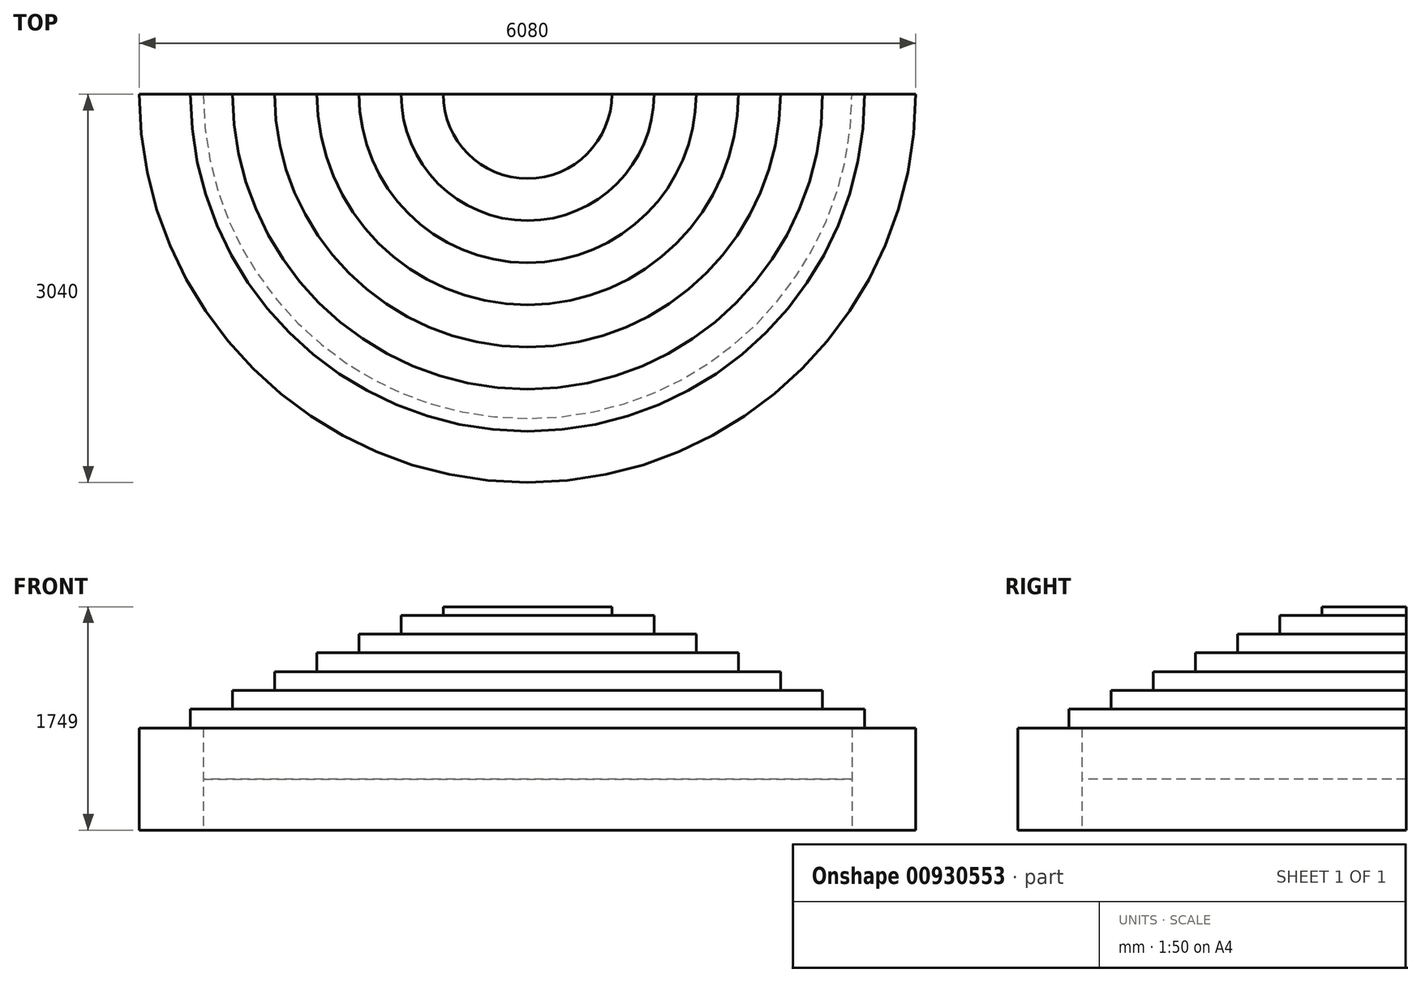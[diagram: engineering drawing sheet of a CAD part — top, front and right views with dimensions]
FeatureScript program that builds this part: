
annotation { "Feature Type Name" : "Feature", "Feature Type Description" : "" }
export const myFeature = defineFeature(function(context is Context, id is Id, definition is map)
    precondition{}
    {
        {
            var Q0;
            Q0=qCreatedBy(makeId("Front.planeOp"),FACE);
            var sketch = newSketch(context, id + "F0", { "sketchPlane" : qUnion([Q0])});
            skLineSegment(sketch, "E0", {"start": v(-660, 882) * mm, "end": v(-990, 882) * mm});
            skLineSegment(sketch, "E1", {"start": v(-990, 882) * mm, "end": v(-990, 735) * mm});
            skLineSegment(sketch, "E2", {"start": v(-990, 735) * mm, "end": v(-1320, 735) * mm});
            skLineSegment(sketch, "E3", {"start": v(-1320, 735) * mm, "end": v(-1320, 588) * mm});
            skLineSegment(sketch, "E4", {"start": v(-1320, 588) * mm, "end": v(-1650, 588) * mm});
            skLineSegment(sketch, "E5", {"start": v(-1650, 588) * mm, "end": v(-1650, 441) * mm});
            skLineSegment(sketch, "E6", {"start": v(-1650, 441) * mm, "end": v(-1980, 441) * mm});
            skLineSegment(sketch, "E7", {"start": v(-1980, 441) * mm, "end": v(-1980, 294) * mm});
            skLineSegment(sketch, "E8", {"start": v(-1980, 294) * mm, "end": v(-2310, 294) * mm});
            skLineSegment(sketch, "E9", {"start": v(-2310, 294) * mm, "end": v(-2310, 147) * mm});
            skLineSegment(sketch, "E10", {"start": v(-2310, 147) * mm, "end": v(-2640, 147) * mm});
            skLineSegment(sketch, "E11", {"start": v(-2640, 147) * mm, "end": v(-2640, 0) * mm});
            skLineSegment(sketch, "E12", {"start": v(-2640, 0) * mm, "end": v(0, 0) * mm});
            skLineSegment(sketch, "E13", {"start": v(0, 0) * mm, "end": v(0, 949) * mm});
            skLineSegment(sketch, "E14", {"start": v(-660, 882) * mm, "end": v(-660, 949) * mm});
            skLineSegment(sketch, "E15", {"start": v(-660, 949) * mm, "end": v(0, 949) * mm});
            skSolve(sketch);
        }
        {
            var Q0;
            Q0 = qSketchRegion(id + "F0", true);
            var Q1;
            Q1=sQuery(id+"F0.wireOp",EDGE,"E13");
            var Q2;
            Q2=sQuery(id+"F0.wireOp",EDGE,"E13");
            revolve(context, id + "F1", {"surfaceOperationType" : NewSurfaceOperationType.NEW, "entities" : qUnion([Q0]), "surfaceEntities" : qUnion([Q1]), "axis" : qUnion([Q2]), "revolveType" : RevolveType.ONE_DIRECTION, "angle" : 180 * degree});
        }
        {
            var Q0;
            Q0=qCreatedBy(makeId("Front.planeOp"),FACE);
            var sketch = newSketch(context, id + "F2", { "sketchPlane" : qUnion([Q0])});
            skLineSegment(sketch, "E16.bottom", {"start": v(-2540, 0) * mm, "end": v(-3040, 0) * mm});
            skLineSegment(sketch, "E16.top", {"start": v(-2540, -800) * mm, "end": v(-3040, -800) * mm});
            skLineSegment(sketch, "E16.left", {"start": v(-2540, 0) * mm, "end": v(-2540, -800) * mm});
            skLineSegment(sketch, "E16.right", {"start": v(-3040, 0) * mm, "end": v(-3040, -800) * mm});
            skSolve(sketch);
        }
        {
            var Q0;
            Q0 = qSketchRegion(id + "F2", true);
            var Q1;
            Q1=sQuery(id+"F0.wireOp",EDGE,"E13");
            revolve(context, id + "F3", {"surfaceOperationType" : NewSurfaceOperationType.NEW, "entities" : qUnion([Q0]), "axis" : qUnion([Q1]), "revolveType" : RevolveType.ONE_DIRECTION, "angle" : 180 * degree});
        }
        {
            var Q0;
            Q0=qCreatedBy(makeId("Front.planeOp"),FACE);
            var sketch = newSketch(context, id + "F4", { "sketchPlane" : qUnion([Q0])});
            skLineSegment(sketch, "E17.bottom", {"start": v(0, 0) * mm, "end": v(-2540, 0) * mm});
            skLineSegment(sketch, "E17.top", {"start": v(0, -400) * mm, "end": v(-2540, -400) * mm});
            skLineSegment(sketch, "E17.left", {"start": v(0, 0) * mm, "end": v(0, -400) * mm});
            skLineSegment(sketch, "E17.right", {"start": v(-2540, 0) * mm, "end": v(-2540, -400) * mm});
            skSolve(sketch);
        }
        {
            var Q0;
            Q0 = qSketchRegion(id + "F4", true);
            var Q1;
            Q1=sQuery(id+"F4.wireOp",EDGE,"E17.left");
            revolve(context, id + "F5", {"surfaceOperationType" : NewSurfaceOperationType.NEW, "entities" : qUnion([Q0]), "axis" : qUnion([Q1]), "revolveType" : RevolveType.ONE_DIRECTION, "oppositeDirection" : true, "angle" : 180 * degree});
        }
    });
